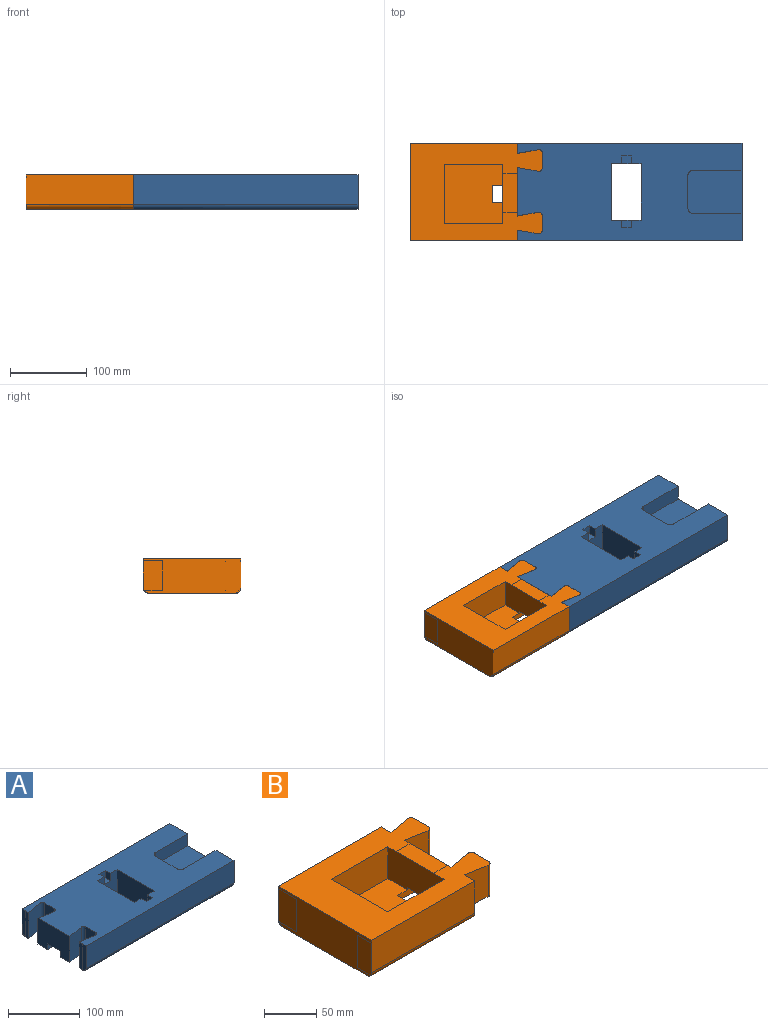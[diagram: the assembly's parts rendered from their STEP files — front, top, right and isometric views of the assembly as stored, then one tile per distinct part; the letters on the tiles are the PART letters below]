
ASSEMBLY  parts=2 mates=1
PART A: 65 faces, bbox 292.1x127x44.5 mm
  f0: plane 12.7x12.7mm, normal (0,1,0), area 161.3mm2, adj f9,f10,f11,f25
  f1: plane 12.7x12.7mm, normal (0,-1,0), area 161.3mm2, adj f6,f7,f8,f25
  f2: plane 44.45x6.86mm, normal (-1,0,0), area 296.3mm2, adj f13,f14,f15,f16,f25
  f3: cylinder r=6.35mm len=20.33mm, axis (0,0,-1), area 202.8mm2, adj f4,f18,f19,f25
  f4: plane 43.18x20.33mm, normal (1,0,0), area 877.8mm2, adj f3,f5,f19,f25
  f5: cylinder r=6.35mm len=20.33mm, axis (0,0,-1), area 202.8mm2, adj f4,f19,f20,f25
  f6: plane 12.7x10.16mm, normal (1,0,0), area 129mm2, adj f1,f8,f25,f28
  f7: plane 12.7x10.16mm, normal (-1,0,0), area 129mm2, adj f1,f8,f25,f28
  f8: plane 12.7x10.16mm, normal (0,0,1), area 129mm2, adj f1,f6,f7,f28
  f9: plane 12.7x10.16mm, normal (1,0,0), area 129mm2, adj f0,f10,f25,f30
  f10: plane 12.7x10.16mm, normal (0,0,1), area 129mm2, adj f0,f9,f11,f30
  f11: plane 12.7x10.16mm, normal (-1,0,0), area 129mm2, adj f0,f10,f25,f30
  f12: plane 122.35x25.18mm, normal (0,0,-1), area 3080.2mm2, adj f27,f31,f32,f33
  f13: plane 38.1x0mm, normal (0,1,0), area 0.1mm2, adj f2,f14,f25,f39
  f14: cylinder r=6.35mm len=6.35mm, axis (-1,0,0), area 0mm2, adj f2,f13,f15,f39
  f15: plane 0.51x0mm, normal (0,0,1), area 0mm2, adj f2,f14,f16,f39
  f16: plane 44.45x0mm, normal (0.17,-0.98,0), area 0.1mm2, adj f2,f15,f25,f39
  f17: plane 292.1x38.1mm, normal (0,-1,0), area 11129mm2, adj f25,f39,f40,f41
  f18: plane 63.95x20.33mm, normal (0,1,0), area 1300.1mm2, adj f3,f19,f25,f41
  f19: plane 70.3x55.88mm, normal (0,0,1), area 3910.6mm2, adj f3,f4,f5,f18,f20,f41
  f20: plane 63.95x20.33mm, normal (0,-1,0), area 1300.1mm2, adj f5,f19,f25,f41
  f21: plane 44.45x6.18mm, normal (-1,0,0), area 266.2mm2, adj f22,f23,f24,f25,f42
  f22: plane 292.1x38.1mm, normal (0,1,0), area 11128.9mm2, adj f21,f25,f41,f42
  f23: cylinder r=6.35mm len=0.06mm, axis (-1,0,0), area 0mm2, adj f21,f24,f42
  f24: plane 44.45x0mm, normal (0.17,0.98,0), area 0.1mm2, adj f21,f23,f25,f43
  f25: plane 292.1x127.01mm, normal (0,0,1), area 28573.2mm2, adj f0,f1,f2,f3,f4,f5,f6,f7
  f26: plane 44.45x27.05mm, normal (0.17,0.98,0), area 1221mm2, adj f25,f33,f47,f48
  f27: plane 122.35x9.96mm, normal (0,-1,0), area 1219mm2, adj f12,f31,f33,f48
  f28: plane 44.45x38.63mm, normal (0,-1,0), area 1556mm2, adj f6,f7,f8,f25,f29,f31,f48
  f29: plane 73.28x44.45mm, normal (-1,0,0), area 3257.2mm2, adj f25,f28,f30,f48
  f30: plane 44.45x38.63mm, normal (0,1,0), area 1556mm2, adj f9,f10,f11,f25,f29,f31,f48
  f31: plane 73.28x44.45mm, normal (1,0,0), area 3006.4mm2, adj f12,f25,f27,f28,f30,f32,f48
  f32: plane 122.35x9.96mm, normal (0,1,0), area 1219mm2, adj f12,f31,f33,f48
  f33: plane 62.98x44.45mm, normal (-1,0,0), area 2548.5mm2, adj f12,f25,f26,f27,f32,f34,f48
  f34: plane 44.45x27.05mm, normal (0.17,-0.98,0), area 1221mm2, adj f25,f33,f35,f48
  f35: cylinder r=4.45mm len=44.45mm, axis (0,0,1), area 344.8mm2, adj f25,f34,f36,f48
  f36: plane 44.45x19.13mm, normal (-1,0,0), area 850.1mm2, adj f25,f35,f37,f48
  f37: cylinder r=4.45mm len=44.45mm, axis (0,0,1), area 344.8mm2, adj f25,f36,f38,f48
  f38: plane 44.45x27.05mm, normal (0.17,0.98,0), area 1221mm2, adj f25,f37,f39,f48
  f39: plane 44.45x14.06mm, normal (-1,0,0), area 320.1mm2, adj f13,f14,f15,f16,f17,f25,f38,f40
  f40: cylinder r=6.35mm len=292.1mm, axis (1,0,0), area 2913.6mm2, adj f17,f39,f41,f48
  f41: plane 127.01x44.45mm, normal (1,0,0), area 4492.1mm2, adj f17,f18,f19,f20,f22,f25,f40,f42
  f42: cylinder r=6.35mm len=292.1mm, axis (-1,0,0), area 2913.5mm2, adj f21,f22,f23,f41,f43,f48
  f43: plane 44.45x7.1mm, normal (-1,0,0), area 315.8mm2, adj f24,f25,f42,f44,f48
  f44: plane 44.45x27.05mm, normal (0.17,-0.98,0), area 1221mm2, adj f25,f43,f45,f48
  f45: cylinder r=4.45mm len=44.45mm, axis (0,0,1), area 344.8mm2, adj f25,f44,f46,f48
  f46: plane 44.45x19.13mm, normal (-1,0,0), area 850.1mm2, adj f25,f45,f47,f48
  f47: cylinder r=4.45mm len=44.45mm, axis (0,0,1), area 344.8mm2, adj f25,f26,f46,f48
  f48: plane 292.1x114.31mm, normal (0,0,-1), area 25952.1mm2, adj f26,f27,f28,f29,f30,f31,f32,f33
  f49: plane 4.12x4.06mm, normal (0,0,-1), area 13mm2, adj f50,f52
  f50: cylinder r=2.03mm len=12.88mm, axis (0,0,-1), area 82.2mm2, adj f49,f51,f52
  f51: plane 4.14x4.06mm, normal (0,0,1), area 13mm2, adj f50,f52
  f52: cylinder r=2.03mm len=12.88mm, axis (0,0,-1), area 82.2mm2, adj f49,f50,f51
  f53: plane 4.12x4.06mm, normal (0,0,-1), area 13mm2, adj f54,f56
  f54: cylinder r=2.03mm len=12.88mm, axis (0,0,-1), area 82.2mm2, adj f53,f55,f56
  f55: plane 4.14x4.06mm, normal (0,0,1), area 13mm2, adj f54,f56
  f56: cylinder r=2.03mm len=12.88mm, axis (0,0,-1), area 82.2mm2, adj f53,f54,f55
  f57: plane 4.12x4.06mm, normal (0,0,-1), area 13mm2, adj f58,f60
  f58: cylinder r=2.03mm len=12.88mm, axis (0,0,-1), area 82.2mm2, adj f57,f59,f60
  f59: plane 4.14x4.06mm, normal (0,0,1), area 13mm2, adj f58,f60
  f60: cylinder r=2.03mm len=12.88mm, axis (0,0,-1), area 82.2mm2, adj f57,f58,f59
  f61: plane 4.12x4.06mm, normal (0,0,-1), area 13mm2, adj f62,f64
  f62: cylinder r=2.03mm len=12.88mm, axis (0,0,-1), area 82.2mm2, adj f61,f63,f64
  f63: plane 4.14x4.06mm, normal (0,0,1), area 13mm2, adj f62,f64
  f64: cylinder r=2.03mm len=12.88mm, axis (0,0,-1), area 82.2mm2, adj f61,f62,f63
PART B: 54 faces, bbox 173.1x128.1x45.6 mm
  f0: plane 76.2x76.2mm, normal (0,0,1), area 5504.4mm2, adj f11,f12,f13,f14,f26,f27,f28
  f1: plane 22.86x18.92mm, normal (0,0,-1), area 432.4mm2, adj f14,f26,f28,f29
  f2: plane 50.8x18.92mm, normal (0,0,1), area 960.9mm2, adj f10,f14,f15,f29
  f3: plane 44.45x0.01mm, normal (-0.17,-0.98,0), area 0.4mm2, adj f7,f34,f35,f37
  f4: plane 38.1x25.17mm, normal (-1,0,0), area 958.4mm2, adj f16,f17,f18,f19,f20,f35
  f5: cylinder r=4.45mm len=39.95mm, axis (0,0,1), area 296.7mm2, adj f6,f32,f33,f37
  f6: plane 41.3x28.15mm, normal (-0.17,0.98,0), area 1057.7mm2, adj f5,f33,f34,f37
  f7: plane 44.45x6.27mm, normal (1,0,0), area 270.2mm2, adj f3,f20,f35,f37
  f8: plane 41.3x28.15mm, normal (-0.17,-0.98,0), area 1057.7mm2, adj f9,f21,f22,f37
  f9: cylinder r=4.45mm len=39.95mm, axis (0,0,1), area 296.7mm2, adj f8,f22,f23,f37
  f10: plane 18.92x0mm, normal (0,-1,0), area 0.1mm2, adj f2,f14,f29,f37
  f11: plane 76.2x37.32mm, normal (0,1,0), area 2843.6mm2, adj f0,f12,f14,f37
  f12: plane 76.2x37.32mm, normal (1,0,0), area 2843.6mm2, adj f0,f11,f13,f37
  f13: plane 76.2x37.32mm, normal (0,-1,0), area 2843.6mm2, adj f0,f12,f14,f37
  f14: plane 76.2x37.32mm, normal (-1,0,0), area 2784.9mm2, adj f0,f1,f2,f10,f11,f13,f15,f26
  f15: plane 18.92x0mm, normal (0,1,0), area 0.1mm2, adj f2,f14,f29,f37
  f16: cylinder r=25.71mm len=2.72mm, axis (1,0,0), area 0.1mm2, adj f4,f17,f35,f42
  f17: plane 21.92x0.02mm, normal (0,0,1), area 0.4mm2, adj f4,f16,f18,f42
  f18: plane 38.1x0.02mm, normal (0,1,0), area 0.8mm2, adj f4,f17,f19,f42
  f19: plane 25.17x0.02mm, normal (0,0,-1), area 0.5mm2, adj f4,f18,f20,f42
  f20: plane 139.7x38.1mm, normal (0,1,0), area 5321.9mm2, adj f4,f7,f19,f35,f37,f42
  f21: plane 44.45x22.14mm, normal (1,0,0), area 336.5mm2, adj f8,f22,f36,f37,f43
  f22: cylinder r=28.7mm len=32.27mm, axis (-1,0,0), area 618.5mm2, adj f8,f9,f21,f23,f43
  f23: plane 44.45x19.13mm, normal (1,0,0), area 827.8mm2, adj f9,f22,f24,f37,f43
  f24: cylinder r=4.45mm len=44.45mm, axis (0,0,1), area 344.8mm2, adj f23,f25,f37,f43
  f25: plane 44.45x27.06mm, normal (-0.17,0.98,0), area 1221.2mm2, adj f24,f29,f37,f43
  f26: plane 32.13x9.71mm, normal (0,1,0), area 277.9mm2, adj f0,f1,f14,f27,f29,f43
  f27: plane 22.86x7.13mm, normal (1,0,0), area 163mm2, adj f0,f26,f28,f43
  f28: plane 32.13x9.71mm, normal (0,-1,0), area 277.9mm2, adj f0,f1,f14,f27,f29,f43
  f29: plane 62.98x44.45mm, normal (1,0,0), area 2577.7mm2, adj f1,f2,f10,f15,f25,f26,f28,f30
  f30: plane 44.45x27.06mm, normal (-0.17,-0.98,0), area 1221.2mm2, adj f29,f31,f37,f43
  f31: cylinder r=4.45mm len=44.45mm, axis (0,0,1), area 344.8mm2, adj f30,f32,f37,f43
  f32: plane 44.45x19.13mm, normal (1,0,0), area 827.8mm2, adj f5,f31,f33,f37,f43
  f33: cylinder r=28.7mm len=32.27mm, axis (1,0,0), area 618.4mm2, adj f5,f6,f32,f34,f43
  f34: plane 44.45x22.14mm, normal (1,0,0), area 336.5mm2, adj f3,f6,f33,f35,f37,f43
  f35: cylinder r=6.35mm len=139.7mm, axis (-1,0,0), area 1393.4mm2, adj f3,f4,f7,f16,f20,f34,f42,f43
  f36: plane 44.45x0.01mm, normal (-0.17,0.98,0), area 0.4mm2, adj f21,f37,f43,f44
  f37: plane 171.96x127mm, normal (0,0,1), area 12499.3mm2, adj f3,f5,f6,f7,f8,f9,f10,f11
  f38: cylinder r=25.71mm len=2.64mm, axis (1,0,0), area 0mm2, adj f39,f42,f46,f47
  f39: plane 15.84x0mm, normal (0,0,-1), area 0mm2, adj f38,f40,f42,f46
  f40: plane 38.17x0mm, normal (0,1,0), area 0mm2, adj f39,f41,f42,f46
  f41: plane 19.5x0mm, normal (0,0,1), area 0mm2, adj f40,f42,f45,f46
  f42: plane 127x44.45mm, normal (-1,0,0), area 3926.7mm2, adj f16,f17,f18,f19,f20,f35,f37,f38
  f43: plane 171.96x114.3mm, normal (0,0,-1), area 15616.8mm2, adj f21,f22,f23,f24,f25,f26,f27,f28
  f44: plane 44.45x6.86mm, normal (1,0,0), area 296.3mm2, adj f36,f37,f43,f45,f47
  f45: plane 139.7x38.1mm, normal (0,-1,0), area 5322.6mm2, adj f37,f41,f42,f44,f46,f47
  f46: plane 38.17x19.5mm, normal (-1,0,0), area 742.7mm2, adj f38,f39,f40,f41,f45,f47
  f47: cylinder r=6.35mm len=139.7mm, axis (-1,0,0), area 1393.4mm2, adj f38,f42,f43,f44,f45,f46
  f48: plane 76.2x38.23mm, normal (0,0,1), area 2912.9mm2, adj f49,f50,f51,f52
  f49: plane 76.2x38.1mm, normal (1,0,0), area 2903.2mm2, adj f48,f50,f52,f53
  f50: plane 38.23x38.1mm, normal (0,1,0), area 1456.4mm2, adj f48,f49,f51,f53
  f51: plane 76.2x38.1mm, normal (-1,0,0), area 2903.2mm2, adj f48,f50,f52,f53
  f52: plane 38.23x38.1mm, normal (0,-1,0), area 1456.4mm2, adj f48,f49,f51,f53
  f53: plane 76.2x38.23mm, normal (0,0,-1), area 2912.9mm2, adj f49,f50,f51,f52
PLACE A t=(55.45,-139.84,39.45)mm
PLACE B t=(-60.37,-71.91,40.92)mm
MATE fastened A.f33 <-> B.f29  axis (-1,0,0) through (-108.34,-51.78,63.37)mm
